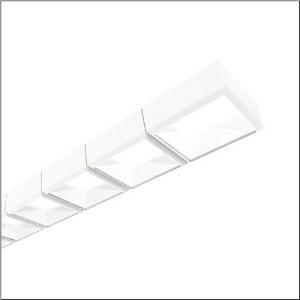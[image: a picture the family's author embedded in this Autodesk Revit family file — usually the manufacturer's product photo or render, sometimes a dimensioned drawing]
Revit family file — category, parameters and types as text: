
# Revit family: scriptus_r__11_5mz323d04wa_1206
name_source: partatom
category: Lighting Fixtures
units: mm (PartAtom-declared; Revit-internal decimal feet)

## family parameters
Cut with Voids When Loaded = No
Host = Face
Light Source = No
Part Type = Normal
Room Calculation Point = No
Round Connector Dimension = Use Diameter
Shared = No

## types (1)
- Scriptus® 11 (1 x LED 4000K / CRI = 80 (unbekannt), 4840 lm / 7230 lm, 4000K)
    Apparent Load = 91 VA
    CIE Flux Codes = - - - 0 100 / 82 95 99 100 100
    Color Rendering = 80
    Color Temperature = 4000K
    Default Elevation = 1800 mm
    Description = Scriptus® 11, office luminaire, primary optical cover: lenses, CAT 2 (L<= 3000cd/m²), light emission: direct/indirect distribution, primary light characteristic: symmetric, installation type: suspended mounting, LED rated luminous flux: 12.070 lm, light colour: 840, colour temperature: 4000K, control gear: ECG DALI, with terminal, 5-pole, mains connection: 230V, AC, 50Hz, rated input power: 91W, LED control gear: ECG DALI, housing, luminaire housing, of aluminium, traffic white (RAL 9016), length: 2.426 mm, width: 114 mm, height: 57mm, protection rating (complete): IP20, insulation class (complete): insulation class I (protective earthing), certification: CE, ENEC, VDE, protection symbol: F, permissible ambient temperature for indoor applications: 0..+35°C, standard: EN 50419, packaging unit: 1 piece
    Height = 57 mm
    Lamp = 1 x LED 4000K / CRI >= 80 (unbekannt)
    Lamp Light Flux = 4840 lm / 7230 lm
    Lamp count = 1
    Length = 2426 mm
    Luminous efficacy = 133 lm/W
    Manufacturer = Siteco
    ModVariant = No
    Model = 5MZ323D04WA
    Mounting Place = Ceiling
    Mounting Type = Pendant
    Number of Poles = 1
    OnlyDefault = Yes
    Power Factor = 1
    Product Name = Scriptus® 11
    Product group = office luminaire | ceiling pendant
    ProductGroupID = 905
    Protection Class = Protection class I
    Protection Degree = IP 20
    RLX_Detail_Level = 1
    RlxData = <blob elided: 30253 chars, md5=6f92dc71>
    Socket = socket
    Standby Power = 0 W
    System Light Flux = 12070 lm
    System Power = 91 W
    Type Comments = Product without accessories
    Type Image = l_1004839.jpg
    URL = http://relux.com
    VarID = ---
    Voltage = 0 V
    Weight = 0.00 kg
    Width = 114 mm

## geometry (parser evidence)
native form markers: Blend x4, Sweep x16
no freeform markers — native parametric forms only
